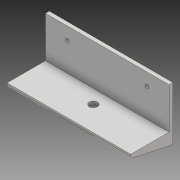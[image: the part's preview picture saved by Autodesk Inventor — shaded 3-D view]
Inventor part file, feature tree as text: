
AUTODESK INVENTOR PART (.ipt)
format: ipt  version: 2018 (Build 220112000, 112)  size: 134,656 bytes
history: native  units: mm
features: extrude x5, sketch x5, other x1, fillet x1
ambient origin geometry x8: Origin, YZ Plane, XZ Plane, XY Plane, X Axis, Y Axis, Z Axis, Center Point
bodies: Body1 (feature_tree), Body2 (feature_tree)
feature tree (12):
  other  "Sólido1"
  extrude  "Extrusión1"  Depth=30.435mm
  extrude  "Extrusión2"  Depth=19.435mm
  extrude  "Extrusión3"  Depth=3.0mm TaperAngle=0.0deg
  extrude  "Extrusión4"  Depth=10.0mm
  extrude  "Extrusión5"  Depth=2.0mm
  fillet  "Empalme1"  Radius=3.0mm
  sketch  "Boceto1"  dims[d0=30.435mm d1=98.0mm]
  sketch  "Boceto2"  dims[d2=3.0mm d3=0.0mm d4=19.435mm]
  sketch  "Boceto3"  dims[d5=6.5mm d6=3.0mm d7=0.0mm]
  sketch  "Boceto4"  dims[d8=35.5mm d9=10.0mm]
  sketch  "Boceto5"  dims[d10=31.5mm d11=31.5mm d12=3.0mm d13=3.0mm d14=3.0mm d15=0.0mm d21=7.0mm d22=30.0mm d23=0.0mm d24=30.0mm d25=0.0mm d26=2.0mm]
